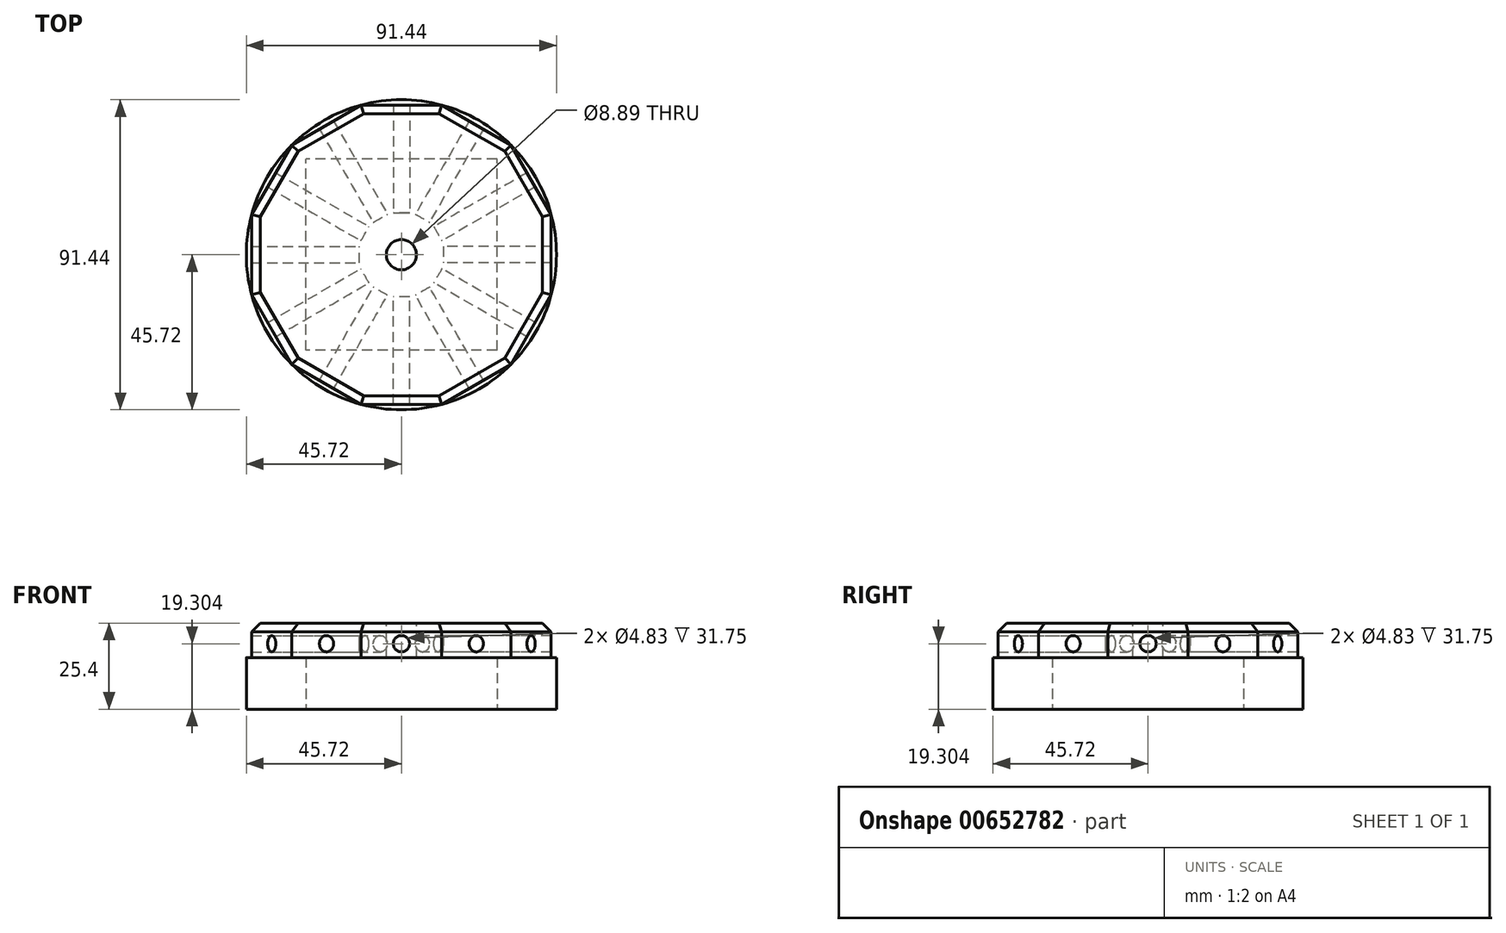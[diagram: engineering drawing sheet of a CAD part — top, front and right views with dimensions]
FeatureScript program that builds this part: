
annotation { "Feature Type Name" : "Feature", "Feature Type Description" : "" }
export const myFeature = defineFeature(function(context is Context, id is Id, definition is map)
    precondition{}
    {
        {
            var Q0;
            Q0=qCreatedBy(makeId("Top.planeOp"),FACE);
            var sketch = newSketch(context, id + "F0", { "sketchPlane" : qUnion([Q0])});
            skCircle(sketch, "E0", {"center": v(0, 0) * mm, "radius": 45.72 * mm});
            skLineSegment(sketch, "E1.bottom", {"start": v(28.2, -28.2) * mm, "end": v(-28.2, -28.2) * mm});
            skLineSegment(sketch, "E1.top", {"start": v(28.2, 28.2) * mm, "end": v(-28.2, 28.2) * mm});
            skLineSegment(sketch, "E1.left", {"start": v(28.2, -28.2) * mm, "end": v(28.2, 28.2) * mm});
            skLineSegment(sketch, "E1.right", {"start": v(-28.2, -28.2) * mm, "end": v(-28.2, 28.2) * mm});
            skSolve(sketch);
        }
        {
            var Q0;
            Q0=makeQuery(id+"F0.imprint","IMPRINT",FACE,{"disambiguationData":[TD([[makeQuery(id+"F0.imprint","IMPRINT",EDGE,{"derivedFrom":sQuery(id+"F0.wireOp",EDGE,"E0")}),1.0]])]});
            extrude(context, id + "F1", {"entities" : qUnion([Q0]), "depth" : 15.24 * mm, "offsetDistance" : 25.4 * mm});
        }
        {
            var Q0;
            Q0=makeQuery(id+"F1.opExtrude","CAP_FACE",FACE,{"disambiguationData":[OSD([sQuery(id+"F0.wireOp",EDGE,"E0"),sQuery(id+"F0.wireOp",EDGE,"E1.bottom"),sQuery(id+"F0.wireOp",EDGE,"E1.top"),sQuery(id+"F0.wireOp",EDGE,"E1.left"),sQuery(id+"F0.wireOp",EDGE,"E1.right")])],"isStart":false});
            var sketch = newSketch(context, id + "F2", { "sketchPlane" : qUnion([Q0])});
            skLineSegment(sketch, "E2", {"start": v(-11.83, 44.16) * mm, "end": v(11.83, 44.16) * mm});
            skLineSegment(sketch, "E3", {"start": v(11.83, 44.16) * mm, "end": v(32.33, 32.33) * mm});
            skLineSegment(sketch, "E4", {"start": v(32.33, 32.33) * mm, "end": v(44.16, 11.83) * mm});
            skLineSegment(sketch, "E5", {"start": v(44.16, 11.83) * mm, "end": v(44.16, -11.83) * mm});
            skLineSegment(sketch, "E6", {"start": v(44.16, -11.83) * mm, "end": v(32.33, -32.33) * mm});
            skLineSegment(sketch, "E7", {"start": v(32.33, -32.33) * mm, "end": v(11.83, -44.16) * mm});
            skLineSegment(sketch, "E8", {"start": v(11.83, -44.16) * mm, "end": v(-11.83, -44.16) * mm});
            skLineSegment(sketch, "E9", {"start": v(-11.83, -44.16) * mm, "end": v(-32.33, -32.33) * mm});
            skLineSegment(sketch, "E10", {"start": v(-32.33, -32.33) * mm, "end": v(-44.16, -11.83) * mm});
            skLineSegment(sketch, "E11", {"start": v(-44.16, -11.83) * mm, "end": v(-44.16, 11.83) * mm});
            skLineSegment(sketch, "E12", {"start": v(-44.16, 11.83) * mm, "end": v(-32.33, 32.33) * mm});
            skLineSegment(sketch, "E13", {"start": v(-32.33, 32.33) * mm, "end": v(-11.83, 44.16) * mm});
            skSolve(sketch);
        }
        {
            var Q0;
            Q0=makeQuery(id+"F2.imprint","IMPRINT",FACE,{"disambiguationData":[TD([[makeQuery(id+"F2.imprint","IMPRINT",EDGE,{"derivedFrom":sQuery(id+"F2.wireOp",EDGE,"E2")}),-1.0]])]});
            extrude(context, id + "F3", {"entities" : qUnion([Q0]), "operationType" : NewBodyOperationType.ADD, "depth" : 10.16 * mm, "offsetDistance" : 25.4 * mm});
        }
        {
            var Q0;
            Q0=makeQuery(id+"F3.opExtrude","CAP_FACE",FACE,{"disambiguationData":[OSD([sQuery(id+"F0.wireOp",EDGE,"E1.bottom"),sQuery(id+"F0.wireOp",EDGE,"E1.top"),sQuery(id+"F0.wireOp",EDGE,"E1.left"),sQuery(id+"F0.wireOp",EDGE,"E1.right"),sQuery(id+"F2.wireOp",EDGE,"E2"),sQuery(id+"F2.wireOp",EDGE,"E3"),sQuery(id+"F2.wireOp",EDGE,"E4"),sQuery(id+"F2.wireOp",EDGE,"E5"),sQuery(id+"F2.wireOp",EDGE,"E6"),sQuery(id+"F2.wireOp",EDGE,"E7"),sQuery(id+"F2.wireOp",EDGE,"E8"),sQuery(id+"F2.wireOp",EDGE,"E9"),sQuery(id+"F2.wireOp",EDGE,"E10"),sQuery(id+"F2.wireOp",EDGE,"E11"),sQuery(id+"F2.wireOp",EDGE,"E12"),sQuery(id+"F2.wireOp",EDGE,"E13")])],"isStart":false});
            var sketch = newSketch(context, id + "F4", { "sketchPlane" : qUnion([Q0])});
            skLineSegment(sketch, "E14.bottom", {"start": v(28.2, 28.2) * mm, "end": v(-28.2, 28.2) * mm});
            skLineSegment(sketch, "E14.top", {"start": v(28.2, -28.2) * mm, "end": v(-28.2, -28.2) * mm});
            skLineSegment(sketch, "E14.left", {"start": v(28.2, 28.2) * mm, "end": v(28.2, -28.2) * mm});
            skLineSegment(sketch, "E14.right", {"start": v(-28.2, 28.2) * mm, "end": v(-28.2, -28.2) * mm});
            skPoint(sketch, "E14.middle", {"position": v(0, 0) * mm});
            skCircle(sketch, "E15", {"center": v(0, 0) * mm, "radius": 4.45 * mm});
            skSolve(sketch);
        }
        {
            var Q0;
            Q0=makeQuery(id+"F4.imprint","IMPRINT",FACE,{"disambiguationData":[TD([[makeQuery(id+"F4.imprint","IMPRINT",EDGE,{"derivedFrom":sQuery(id+"F4.wireOp",EDGE,"E14.bottom")}),1.0]])]});
            extrude(context, id + "F5", {"entities" : qUnion([Q0]), "operationType" : NewBodyOperationType.ADD, "oppositeDirection" : true, "depth" : 10.16 * mm, "offsetDistance" : 25.4 * mm});
        }
        {
            var Q0;
            Q0=makeQuery(id+"F3.opExtrude","SWEPT_FACE",FACE,{"disambiguationData":[OSD([sQuery(id+"F2.wireOp",EDGE,"E10")])]});
            var sketch = newSketch(context, id + "F6", { "sketchPlane" : qUnion([Q0])});
            skCircle(sketch, "E16", {"center": v(0, 19.3) * mm, "radius": 2.41 * mm});
            skPoint(sketch, "E16.centerSnap0", {"position": v(0, 15.24) * mm});
            skSolve(sketch);
        }
        {
            var Q0;
            Q0=makeQuery(id+"F6.imprint","IMPRINT",FACE,{"disambiguationData":[TD([[makeQuery(id+"F6.imprint","IMPRINT",EDGE,{"derivedFrom":sQuery(id+"F6.wireOp",EDGE,"E16")}),1.0]])]});
            extrude(context, id + "F7", {"entities" : qUnion([Q0]), "endBound" : BoundingType.SYMMETRIC, "depth" : 63.5 * mm, "offsetDistance" : 25.4 * mm});
        }
        {
            var Q0;
            Q0=makeQuery(id+"F7.opExtrude","SWEPT_BODY",BODY,{"disambiguationData":[OSD([sQuery(id+"F6.wireOp",EDGE,"E16")])]});
            var Q1;
            Q1=makeQuery(id+"F5.opExtrude","CAP_EDGE",EDGE,{"disambiguationData":[OSD([sQuery(id+"F4.wireOp",EDGE,"E15")])],"isStart":true});
            circularPattern(context, id + "F8", {"entities" : qUnion([Q0]), "axis" : qUnion([Q1]), "angle" : 360 * degree, "instanceCount" : 12, "equalSpace" : true});
        }
        {
            var Q0;
            Q0=makeQuery(id+"F3.opExtrude","CAP_EDGE",EDGE,{"disambiguationData":[OSD([sQuery(id+"F2.wireOp",EDGE,"E4")])],"isStart":false});
            var Q1;
            Q1=makeQuery(id+"F3.opExtrude","CAP_EDGE",EDGE,{"disambiguationData":[OSD([sQuery(id+"F2.wireOp",EDGE,"E3")])],"isStart":false});
            var Q2;
            Q2=makeQuery(id+"F3.opExtrude","CAP_EDGE",EDGE,{"disambiguationData":[OSD([sQuery(id+"F2.wireOp",EDGE,"E2")])],"isStart":false});
            var Q3;
            Q3=makeQuery(id+"F3.opExtrude","CAP_EDGE",EDGE,{"disambiguationData":[OSD([sQuery(id+"F2.wireOp",EDGE,"E5")])],"isStart":false});
            var Q4;
            Q4=makeQuery(id+"F3.opExtrude","CAP_EDGE",EDGE,{"disambiguationData":[OSD([sQuery(id+"F2.wireOp",EDGE,"E6")])],"isStart":false});
            var Q5;
            Q5=makeQuery(id+"F3.opExtrude","CAP_EDGE",EDGE,{"disambiguationData":[OSD([sQuery(id+"F2.wireOp",EDGE,"E7")])],"isStart":false});
            var Q6;
            Q6=makeQuery(id+"F3.opExtrude","CAP_EDGE",EDGE,{"disambiguationData":[OSD([sQuery(id+"F2.wireOp",EDGE,"E8")])],"isStart":false});
            var Q7;
            Q7=makeQuery(id+"F3.opExtrude","CAP_EDGE",EDGE,{"disambiguationData":[OSD([sQuery(id+"F2.wireOp",EDGE,"E9")])],"isStart":false});
            var Q8;
            Q8=makeQuery(id+"F3.opExtrude","CAP_EDGE",EDGE,{"disambiguationData":[OSD([sQuery(id+"F2.wireOp",EDGE,"E10")])],"isStart":false});
            var Q9;
            Q9=makeQuery(id+"F3.opExtrude","CAP_EDGE",EDGE,{"disambiguationData":[OSD([sQuery(id+"F2.wireOp",EDGE,"E11")])],"isStart":false});
            var Q10;
            Q10=makeQuery(id+"F3.opExtrude","CAP_EDGE",EDGE,{"disambiguationData":[OSD([sQuery(id+"F2.wireOp",EDGE,"E12")])],"isStart":false});
            var Q11;
            Q11=makeQuery(id+"F3.opExtrude","CAP_EDGE",EDGE,{"disambiguationData":[OSD([sQuery(id+"F2.wireOp",EDGE,"E13")])],"isStart":false});
            chamfer(context, id + "F9", {"entities" : qUnion([Q0, Q1, Q2, Q3, Q4, Q5, Q6, Q7, Q8, Q9, Q10, Q11]), "width" : 2.54 * mm, "tangentPropagation" : true});
        }
        {
            var Q0;
            Q0=makeQuery(id+"F8.opPattern","COPY",BODY,{"derivedFrom":makeQuery(id+"F7.opExtrude","SWEPT_BODY",BODY,{"disambiguationData":[OSD([sQuery(id+"F6.wireOp",EDGE,"E16")])]}),"instanceName":"2"});
            var Q1;
            Q1=makeQuery(id+"F8.opPattern","COPY",BODY,{"derivedFrom":makeQuery(id+"F7.opExtrude","SWEPT_BODY",BODY,{"disambiguationData":[OSD([sQuery(id+"F6.wireOp",EDGE,"E16")])]}),"instanceName":"1"});
            var Q2;
            Q2=makeQuery(id+"F7.opExtrude","SWEPT_BODY",BODY,{"disambiguationData":[OSD([sQuery(id+"F6.wireOp",EDGE,"E16")])]});
            var Q3;
            Q3=makeQuery(id+"F8.opPattern","COPY",BODY,{"derivedFrom":makeQuery(id+"F7.opExtrude","SWEPT_BODY",BODY,{"disambiguationData":[OSD([sQuery(id+"F6.wireOp",EDGE,"E16")])]}),"instanceName":"11"});
            var Q4;
            Q4=makeQuery(id+"F8.opPattern","COPY",BODY,{"derivedFrom":makeQuery(id+"F7.opExtrude","SWEPT_BODY",BODY,{"disambiguationData":[OSD([sQuery(id+"F6.wireOp",EDGE,"E16")])]}),"instanceName":"10"});
            var Q5;
            Q5=makeQuery(id+"F8.opPattern","COPY",BODY,{"derivedFrom":makeQuery(id+"F7.opExtrude","SWEPT_BODY",BODY,{"disambiguationData":[OSD([sQuery(id+"F6.wireOp",EDGE,"E16")])]}),"instanceName":"9"});
            var Q6;
            Q6=makeQuery(id+"F8.opPattern","COPY",BODY,{"derivedFrom":makeQuery(id+"F7.opExtrude","SWEPT_BODY",BODY,{"disambiguationData":[OSD([sQuery(id+"F6.wireOp",EDGE,"E16")])]}),"instanceName":"8"});
            var Q7;
            Q7=makeQuery(id+"F8.opPattern","COPY",BODY,{"derivedFrom":makeQuery(id+"F7.opExtrude","SWEPT_BODY",BODY,{"disambiguationData":[OSD([sQuery(id+"F6.wireOp",EDGE,"E16")])]}),"instanceName":"7"});
            var Q8;
            Q8=makeQuery(id+"F8.opPattern","COPY",BODY,{"derivedFrom":makeQuery(id+"F7.opExtrude","SWEPT_BODY",BODY,{"disambiguationData":[OSD([sQuery(id+"F6.wireOp",EDGE,"E16")])]}),"instanceName":"6"});
            var Q9;
            Q9=makeQuery(id+"F8.opPattern","COPY",BODY,{"derivedFrom":makeQuery(id+"F7.opExtrude","SWEPT_BODY",BODY,{"disambiguationData":[OSD([sQuery(id+"F6.wireOp",EDGE,"E16")])]}),"instanceName":"5"});
            var Q10;
            Q10=makeQuery(id+"F8.opPattern","COPY",BODY,{"derivedFrom":makeQuery(id+"F7.opExtrude","SWEPT_BODY",BODY,{"disambiguationData":[OSD([sQuery(id+"F6.wireOp",EDGE,"E16")])]}),"instanceName":"4"});
            var Q11;
            Q11=makeQuery(id+"F8.opPattern","COPY",BODY,{"derivedFrom":makeQuery(id+"F7.opExtrude","SWEPT_BODY",BODY,{"disambiguationData":[OSD([sQuery(id+"F6.wireOp",EDGE,"E16")])]}),"instanceName":"3"});
            var Q12;
            Q12=makeQuery(id+"F1.opExtrude","SWEPT_BODY",BODY,{"disambiguationData":[OSD([sQuery(id+"F0.wireOp",EDGE,"E0"),sQuery(id+"F0.wireOp",EDGE,"E1.bottom"),sQuery(id+"F0.wireOp",EDGE,"E1.top"),sQuery(id+"F0.wireOp",EDGE,"E1.left"),sQuery(id+"F0.wireOp",EDGE,"E1.right")])]});
            booleanBodies(context, id + "F10", {"operationType" : BooleanOperationType.SUBTRACTION, "tools" : qUnion([Q0, Q1, Q2, Q3, Q4, Q5, Q6, Q7, Q8, Q9, Q10, Q11]), "targets" : qUnion([Q12])});
        }
    });
